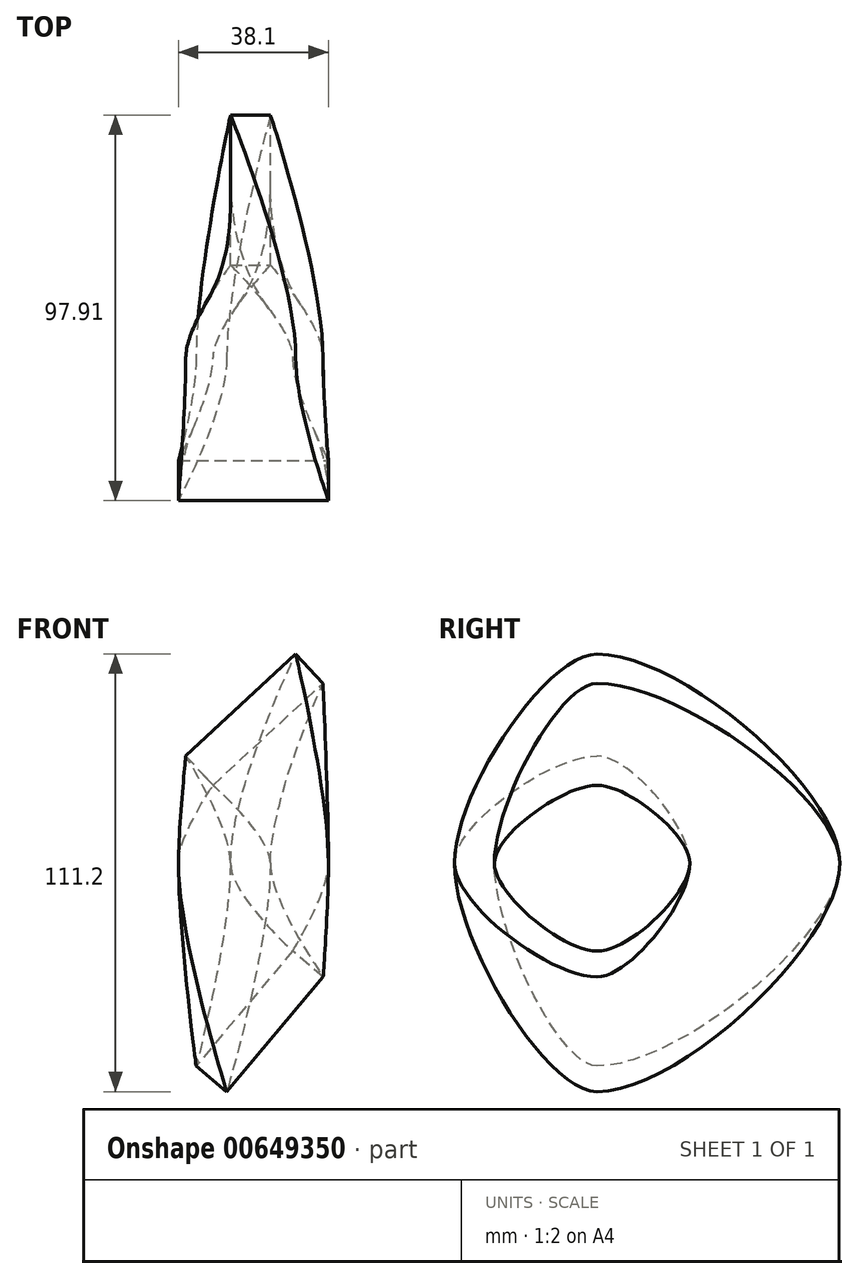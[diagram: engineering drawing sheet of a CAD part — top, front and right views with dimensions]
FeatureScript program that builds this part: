
annotation { "Feature Type Name" : "Feature", "Feature Type Description" : "" }
export const myFeature = defineFeature(function(context is Context, id is Id, definition is map)
    precondition{}
    {
        {
            var Q0;
            Q0=qCreatedBy(makeId("Top.planeOp"),FACE);
            var sketch = newSketch(context, id + "F0", { "sketchPlane" : qUnion([Q0])});
            skLineSegment(sketch, "E0.bottom", {"start": v(-19.6, -26.12) * mm, "end": v(18.5, -26.12) * mm});
            skLineSegment(sketch, "E0.top", {"start": v(-19.6, -36.28) * mm, "end": v(18.5, -36.28) * mm});
            skLineSegment(sketch, "E0.left", {"start": v(-19.6, -26.12) * mm, "end": v(-19.6, -36.28) * mm});
            skLineSegment(sketch, "E0.right", {"start": v(18.5, -26.12) * mm, "end": v(18.5, -36.28) * mm});
            skSolve(sketch);
        }
        {
            var Q0;
            Q0=qCreatedBy(makeId("Front.planeOp"),FACE);
            var sketch = newSketch(context, id + "F1", { "sketchPlane" : qUnion([Q0])});
            skLineSegment(sketch, "E1.bottom", {"start": v(-17.73, 27.22) * mm, "end": v(10.2, 53.14) * mm});
            skLineSegment(sketch, "E1.top", {"start": v(-10.82, 19.77) * mm, "end": v(17.1, 45.7) * mm});
            skLineSegment(sketch, "E1.left", {"start": v(-17.73, 27.22) * mm, "end": v(-10.82, 19.77) * mm});
            skLineSegment(sketch, "E1.right", {"start": v(10.2, 53.14) * mm, "end": v(17.1, 45.7) * mm});
            skSolve(sketch);
        }
        {
            var Q0;
            Q0=makeQuery(id+"F0.imprint","IMPRINT",FACE,{"disambiguationData":[TD([[makeQuery(id+"F0.imprint","IMPRINT",EDGE,{"derivedFrom":sQuery(id+"F0.wireOp",EDGE,"E0.bottom")}),-1.0]])]});
            var Q1;
            Q1=makeQuery(id+"F1.imprint","IMPRINT",FACE,{"disambiguationData":[TD([[makeQuery(id+"F1.imprint","IMPRINT",EDGE,{"derivedFrom":sQuery(id+"F1.wireOp",EDGE,"E1.bottom")}),-1.0]])]});
            loft(context, id + "F2", {"startCondition" : LoftEndDerivativeType.NORMAL_TO_PROFILE, "startMagnitude" : 1, "endCondition" : LoftEndDerivativeType.NORMAL_TO_PROFILE, "endMagnitude" : 1, "sheetProfilesArray" : [{ "sheetProfileEntities" : qUnion([Q0]) }, { "sheetProfileEntities" : qUnion([Q1]) }]});
        }
        {
            var Q0;
            Q0=qCreatedBy(makeId("Top.planeOp"),FACE);
            var sketch = newSketch(context, id + "F3", { "sketchPlane" : qUnion([Q0])});
            skLineSegment(sketch, "E2.bottom", {"start": v(-6.4, 23.53) * mm, "end": v(-6.4, 61.63) * mm});
            skLineSegment(sketch, "E2.top", {"start": v(3.77, 23.53) * mm, "end": v(3.77, 61.63) * mm});
            skLineSegment(sketch, "E2.left", {"start": v(-6.4, 23.53) * mm, "end": v(3.77, 23.53) * mm});
            skLineSegment(sketch, "E2.right", {"start": v(-6.4, 61.63) * mm, "end": v(3.77, 61.63) * mm});
            skSolve(sketch);
        }
        {
            var Q1;
            Q1=makeQuery(id+"F3.imprint","IMPRINT",FACE,{"disambiguationData":[TD([[makeQuery(id+"F3.imprint","IMPRINT",EDGE,{"derivedFrom":sQuery(id+"F3.wireOp",EDGE,"E2.bottom")}),-1.0]])]});
            var Q2;
            Q2=makeQuery(id+"F2.opLoft","CAP_FACE",FACE,{"disambiguationData":[OSD([makeQuery(id+"F1.imprint","IMPRINT",FACE,{"disambiguationData":[TD([[makeQuery(id+"F1.imprint","IMPRINT",EDGE,{"derivedFrom":sQuery(id+"F1.wireOp",EDGE,"E1.bottom")}),-1.0]])]})])],"isStart":true});
            var Q3;
            Q3=makeQuery(id+"F2.opLoft","MID_CAP_VERTEX",VERTEX,{"disambiguationData":[OSD([sQuery(id+"F1.wireOp",EDGE,"E1.bottom"),sQuery(id+"F1.wireOp",EDGE,"E1.right")])],"capPos":1.0});
            var Q4;
            Q4=sQuery(id+"F3.wireOp",VERTEX,"E2.right.start");
            loft(context, id + "F4", {"operationType" : NewBodyOperationType.ADD, "startCondition" : LoftEndDerivativeType.NORMAL_TO_PROFILE, "startMagnitude" : 1, "endCondition" : LoftEndDerivativeType.NORMAL_TO_PROFILE, "endMagnitude" : 1, "sheetProfilesArray" : [{ "sheetProfileEntities" : qUnion([Q1]) }, { "sheetProfileEntities" : qUnion([Q2]) }], "matchConnections" : true, "connections" : [{ "connectionEntities" : qUnion([Q3, Q4]), "connectionEdgeQueries" : qUnion([]), "connectionEdgeParameters" : [] }]});
        }
        {
            var Q0;
            Q0=qCreatedBy(makeId("Front.planeOp"),FACE);
            var sketch = newSketch(context, id + "F5", { "sketchPlane" : qUnion([Q0])});
            skLineSegment(sketch, "E3.bottom", {"start": v(17.17, -28.88) * mm, "end": v(-7.32, -58.06) * mm});
            skLineSegment(sketch, "E3.top", {"start": v(9.39, -22.35) * mm, "end": v(-15.1, -51.53) * mm});
            skLineSegment(sketch, "E3.left", {"start": v(17.17, -28.88) * mm, "end": v(9.39, -22.35) * mm});
            skLineSegment(sketch, "E3.right", {"start": v(-7.32, -58.06) * mm, "end": v(-15.1, -51.53) * mm});
            skSolve(sketch);
        }
        {
            var Q1;
            Q1=makeQuery(id+"F4.opLoft","CAP_FACE",FACE,{"disambiguationData":[OSD([makeQuery(id+"F3.imprint","IMPRINT",FACE,{"disambiguationData":[TD([[makeQuery(id+"F3.imprint","IMPRINT",EDGE,{"derivedFrom":sQuery(id+"F3.wireOp",EDGE,"E2.bottom")}),-1.0]])]})])],"isStart":true});
            var Q2;
            Q2=makeQuery(id+"F5.imprint","IMPRINT",FACE,{"disambiguationData":[TD([[makeQuery(id+"F5.imprint","IMPRINT",EDGE,{"derivedFrom":sQuery(id+"F5.wireOp",EDGE,"E3.bottom")}),-1.0]])]});
            loft(context, id + "F6", {"operationType" : NewBodyOperationType.ADD, "startCondition" : LoftEndDerivativeType.NORMAL_TO_PROFILE, "startMagnitude" : 1, "endCondition" : LoftEndDerivativeType.NORMAL_TO_PROFILE, "endMagnitude" : 1, "sheetProfilesArray" : [{ "sheetProfileEntities" : qUnion([Q1]) }, { "sheetProfileEntities" : qUnion([Q2]) }]});
        }
        {
            var Q1;
            Q1=makeQuery(id+"F6.opLoft","CAP_FACE",FACE,{"disambiguationData":[OSD([makeQuery(id+"F5.imprint","IMPRINT",FACE,{"disambiguationData":[TD([[makeQuery(id+"F5.imprint","IMPRINT",EDGE,{"derivedFrom":sQuery(id+"F5.wireOp",EDGE,"E3.bottom")}),-1.0]])]})])],"isStart":true});
            var Q2;
            Q2=makeQuery(id+"F2.opLoft","CAP_FACE",FACE,{"disambiguationData":[OSD([makeQuery(id+"F0.imprint","IMPRINT",FACE,{"disambiguationData":[TD([[makeQuery(id+"F0.imprint","IMPRINT",EDGE,{"derivedFrom":sQuery(id+"F0.wireOp",EDGE,"E0.bottom")}),-1.0]])]})])],"isStart":true});
            loft(context, id + "F7", {"operationType" : NewBodyOperationType.ADD, "startCondition" : LoftEndDerivativeType.NORMAL_TO_PROFILE, "startMagnitude" : 1, "endCondition" : LoftEndDerivativeType.NORMAL_TO_PROFILE, "endMagnitude" : 1, "sheetProfilesArray" : [{ "sheetProfileEntities" : qUnion([Q1]) }, { "sheetProfileEntities" : qUnion([Q2]) }]});
        }
    });
